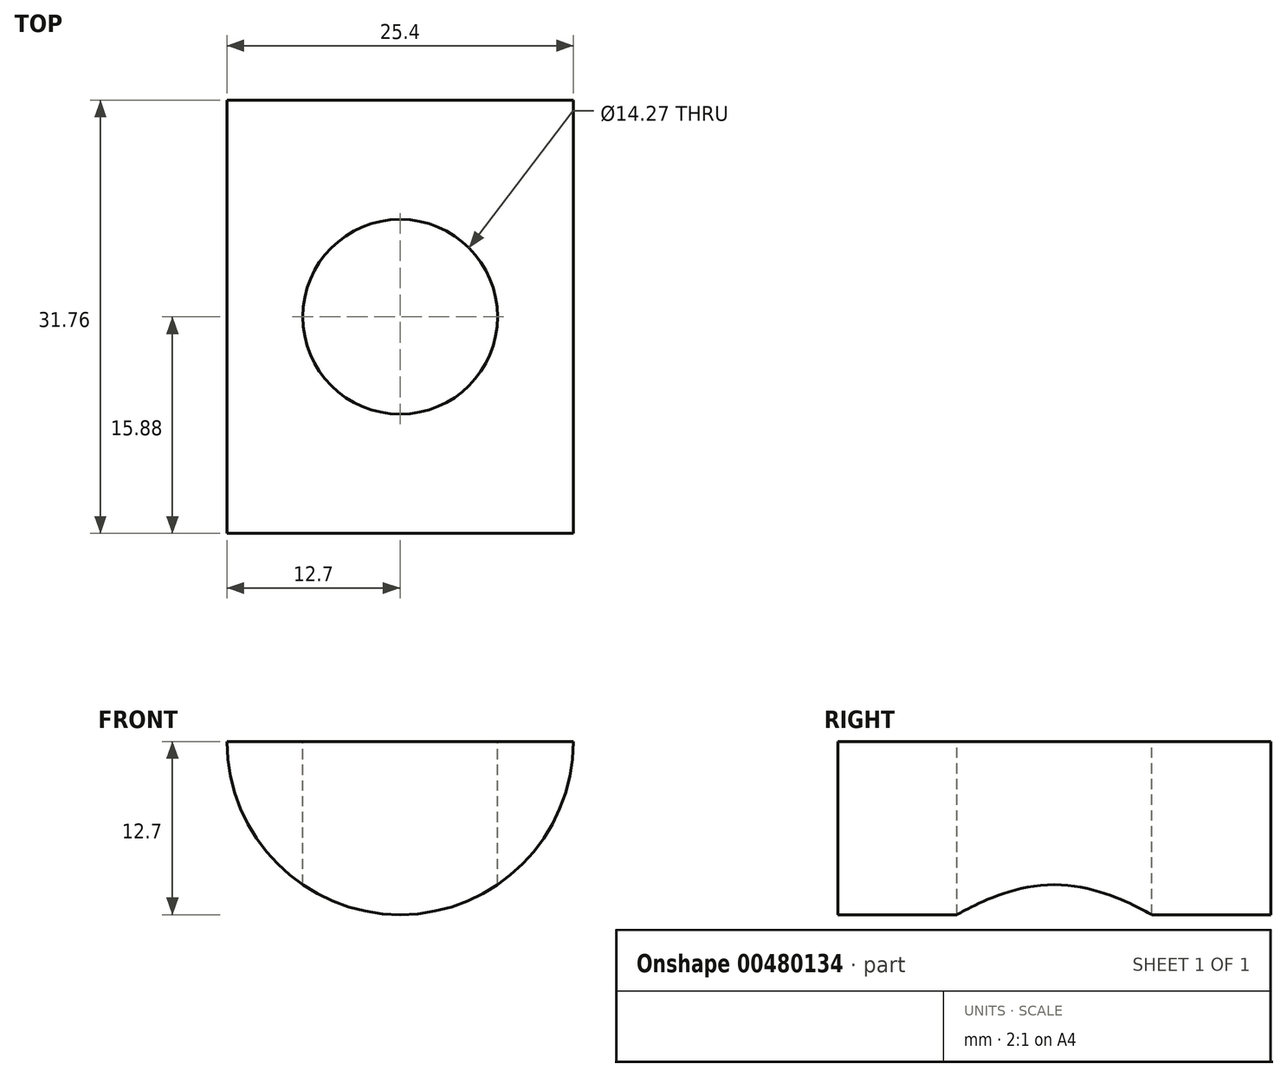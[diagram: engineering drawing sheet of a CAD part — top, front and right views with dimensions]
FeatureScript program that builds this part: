
annotation { "Feature Type Name" : "Feature", "Feature Type Description" : "" }
export const myFeature = defineFeature(function(context is Context, id is Id, definition is map)
    precondition{}
    {
        {
            var Q0;
            Q0=qCreatedBy(makeId("Front.planeOp"),FACE);
            var sketch = newSketch(context, id + "F0", { "sketchPlane" : qUnion([Q0])});
            skArc(sketch, "E0", {"start": v(-12.7, 0) * mm, "mid": v(0, -12.7) * mm, "end": v(12.7, 0) * mm});
            skLineSegment(sketch, "E1", {"start": v(-12.7, 0) * mm, "end": v(12.7, 0) * mm});
            skSolve(sketch);
        }
        {
            var Q0;
            Q0 = qSketchRegion(id + "F0", true);
            extrude(context, id + "F1", {"entities" : qUnion([Q0]), "endBound" : BoundingType.SYMMETRIC, "depth" : 31.75 * mm});
        }
        {
            var Q0;
            Q0=makeQuery(id+"F1.opExtrude","SWEPT_FACE",FACE,{"disambiguationData":[OSD([sQuery(id+"F0.wireOp",EDGE,"E1")])]});
            var sketch = newSketch(context, id + "F2", { "sketchPlane" : qUnion([Q0])});
            skCircle(sketch, "E2", {"center": v(0, 0) * mm, "radius": 7.14 * mm});
            skSolve(sketch);
        }
        {
            var Q0;
            Q0 = qSketchRegion(id + "F2", true);
            extrude(context, id + "F3", {"entities" : qUnion([Q0]), "operationType" : NewBodyOperationType.REMOVE, "oppositeDirection" : true, "depth" : 25.4 * mm});
        }
    });
